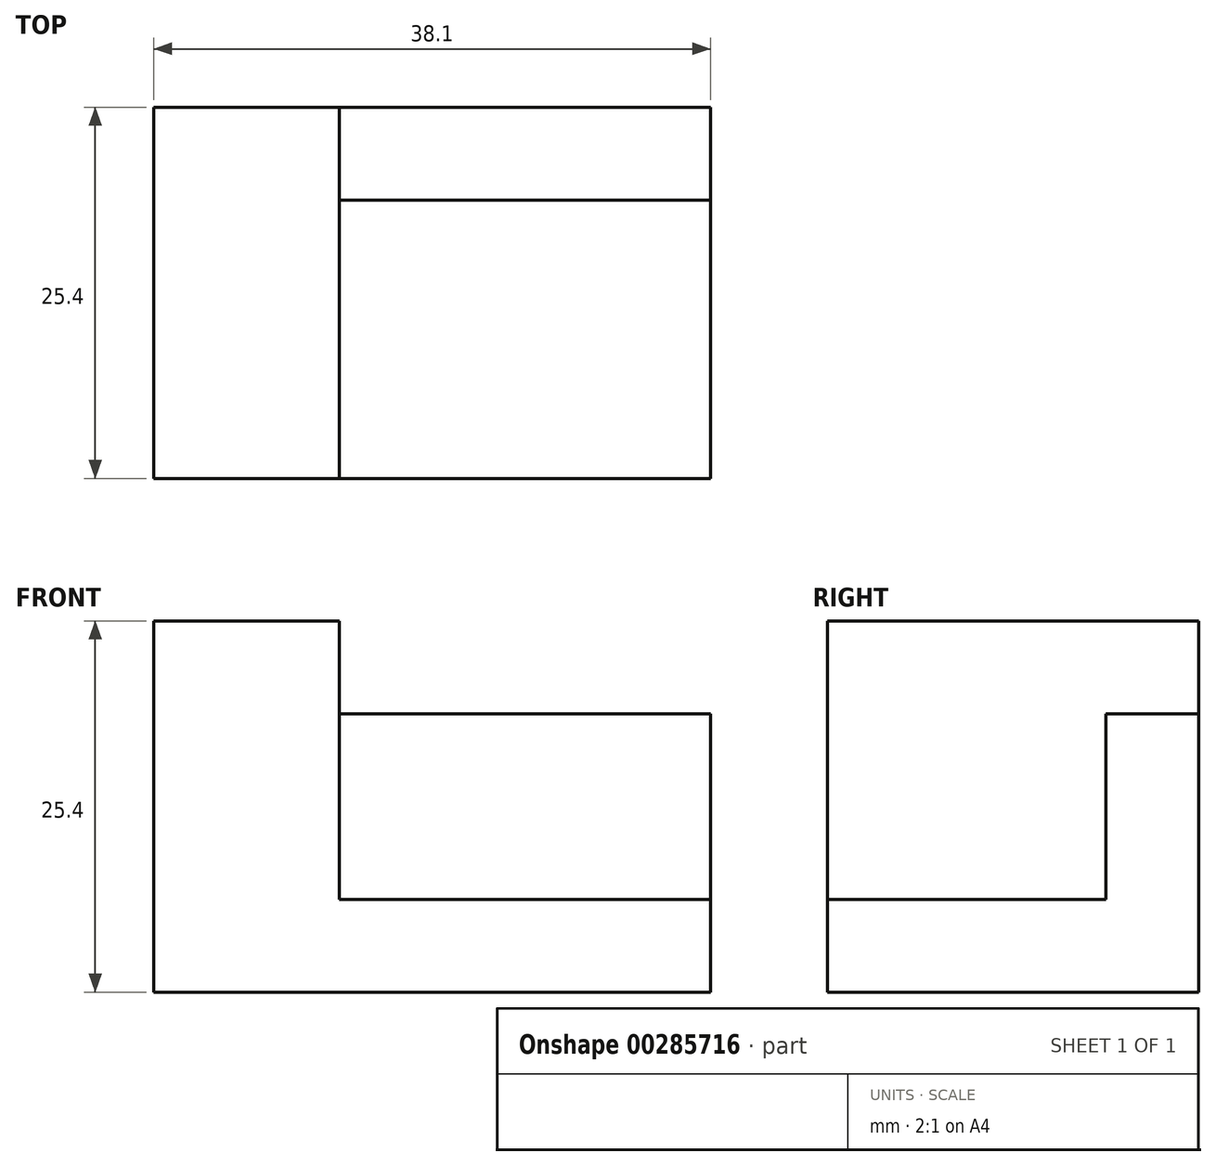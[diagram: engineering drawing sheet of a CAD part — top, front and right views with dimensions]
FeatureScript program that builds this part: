
annotation { "Feature Type Name" : "Feature", "Feature Type Description" : "" }
export const myFeature = defineFeature(function(context is Context, id is Id, definition is map)
    precondition{}
    {
        {
            var Q0;
            Q0=qCreatedBy(makeId("Front.planeOp"),FACE);
            var sketch = newSketch(context, id + "F0", { "sketchPlane" : qUnion([Q0])});
            skLineSegment(sketch, "E0", {"start": v(0, 0) * mm, "end": v(0, 25.4) * mm});
            skLineSegment(sketch, "E1", {"start": v(0, 25.4) * mm, "end": v(12.7, 25.4) * mm});
            skLineSegment(sketch, "E2", {"start": v(12.7, 25.4) * mm, "end": v(12.7, 6.35) * mm});
            skLineSegment(sketch, "E3", {"start": v(12.7, 6.35) * mm, "end": v(38.1, 6.35) * mm});
            skLineSegment(sketch, "E4", {"start": v(38.1, 6.35) * mm, "end": v(38.1, 0) * mm});
            skLineSegment(sketch, "E5", {"start": v(38.1, 0) * mm, "end": v(0, 0) * mm});
            skLineSegment(sketch, "E6", {"start": v(38.1, 6.35) * mm, "end": v(38.1, 19.05) * mm});
            skLineSegment(sketch, "E7", {"start": v(38.1, 19.05) * mm, "end": v(12.7, 19.05) * mm});
            skPoint(sketch, "E7.endSnap0", {"position": v(12.7, 15.88) * mm});
            skLineSegment(sketch, "E8", {"start": v(12.7, 19.05) * mm, "end": v(12.7, 6.35) * mm});
            skSolve(sketch);
        }
        {
            var Q0;
            Q0 = qSketchRegion(id + "F0", true);
            extrude(context, id + "F1", {"entities" : qUnion([Q0]), "depth" : 25.4 * mm});
        }
        {
            var Q0;
            Q0=makeQuery(id+"F1.opExtrude","SWEPT_FACE",FACE,{"disambiguationData":[OSD([sQuery(id+"F0.wireOp",EDGE,"E4"),sQuery(id+"F0.wireOp",EDGE,"E6")])]});
            var sketch = newSketch(context, id + "F2", { "sketchPlane" : qUnion([Q0])});
            skLineSegment(sketch, "E9", {"start": v(0, 19.05) * mm, "end": v(-6.35, 19.05) * mm});
            skLineSegment(sketch, "E10", {"start": v(-6.35, 19.05) * mm, "end": v(-6.35, 6.35) * mm});
            skLineSegment(sketch, "E11", {"start": v(-6.35, 6.35) * mm, "end": v(-25.4, 6.35) * mm});
            skLineSegment(sketch, "E12", {"start": v(-25.4, 6.35) * mm, "end": v(-25.4, 0) * mm});
            skLineSegment(sketch, "E13", {"start": v(-25.4, 0) * mm, "end": v(0, 0) * mm});
            skLineSegment(sketch, "E14", {"start": v(0, 0) * mm, "end": v(0, 19.05) * mm});
            skLineSegment(sketch, "E15", {"start": v(0, 19.05) * mm, "end": v(-25.4, 19.05) * mm});
            skLineSegment(sketch, "E16", {"start": v(-25.4, 19.05) * mm, "end": v(-25.4, 6.35) * mm});
            skSolve(sketch);
        }
        {
            var Q0;
            {var subQ0=sQuery(id+"F2.wireOp",EDGE,"E10");Q0=makeQuery(id+"F2.imprint","IMPRINT",FACE,{"disambiguationData":[TD([[makeQuery(id+"F2.imprint","IMPRINT",EDGE,{"derivedFrom":subQ0}),-1.0]])]});}
            extrude(context, id + "F3", {"entities" : qUnion([Q0]), "operationType" : NewBodyOperationType.REMOVE, "oppositeDirection" : true, "depth" : 25.4 * mm});
        }
    });
